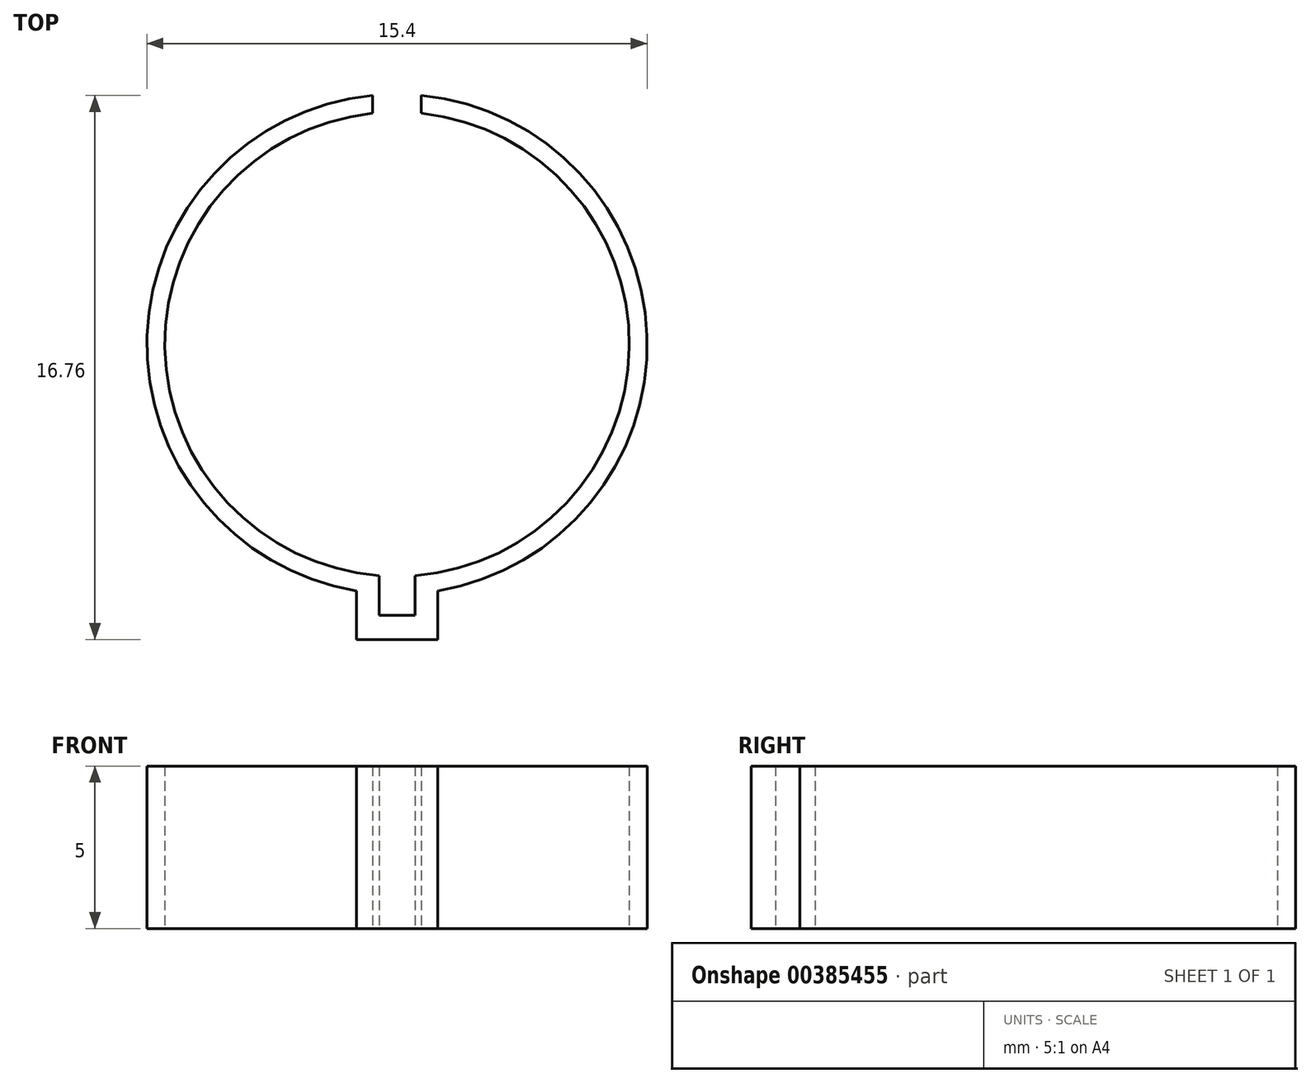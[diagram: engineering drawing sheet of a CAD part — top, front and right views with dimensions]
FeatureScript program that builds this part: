
annotation { "Feature Type Name" : "Feature", "Feature Type Description" : "" }
export const myFeature = defineFeature(function(context is Context, id is Id, definition is map)
    precondition{}
    {
        {
            var Q0;
            Q0=qCreatedBy(makeId("Top.planeOp"),FACE);
            var sketch = newSketch(context, id + "F0", { "sketchPlane" : qUnion([Q0])});
            skCircle(sketch, "E0", {"center": v(0, 0) * mm, "radius": 7.15 * mm});
            skCircle(sketch, "E1", {"center": v(0, 0) * mm, "radius": 7.7 * mm});
            skLineSegment(sketch, "E2", {"start": v(-0.75, 7.11) * mm, "end": v(-0.75, 7.66) * mm});
            skLineSegment(sketch, "E3", {"start": v(0.75, 7.11) * mm, "end": v(0.75, 7.66) * mm});
            skLineSegment(sketch, "E4", {"start": v(-1.25, -7.6) * mm, "end": v(-1.25, -9.1) * mm});
            skLineSegment(sketch, "E5", {"start": v(-1.25, -9.1) * mm, "end": v(1.25, -9.1) * mm});
            skLineSegment(sketch, "E6", {"start": v(1.25, -9.1) * mm, "end": v(1.25, -7.6) * mm});
            skLineSegment(sketch, "E7", {"start": v(-0.55, -7.68) * mm, "end": v(-0.55, -8.35) * mm});
            skPoint(sketch, "E7.endSnap0", {"position": v(-1.25, -8.35) * mm});
            skLineSegment(sketch, "E8", {"start": v(-0.55, -8.35) * mm, "end": v(0.55, -8.35) * mm});
            skPoint(sketch, "E8.endSnap0", {"position": v(1.25, -8.35) * mm});
            skLineSegment(sketch, "E9", {"start": v(0.55, -8.35) * mm, "end": v(0.55, -7.6) * mm});
            skLineSegment(sketch, "E10", {"start": v(0.55, -7.6) * mm, "end": v(0.55, -7.13) * mm});
            skLineSegment(sketch, "E11", {"start": v(-0.55, -7.68) * mm, "end": v(-0.55, -7.13) * mm});
            skSolve(sketch);
        }
        {
            var Q0;
            {var subQ4=sQuery(id+"F0.wireOp",EDGE,"E2");Q0=makeQuery(id+"F0.imprint","IMPRINT",FACE,{"disambiguationData":[TD([[makeQuery(id+"F0.imprint","IMPRINT",EDGE,{"derivedFrom":subQ4}),1.0]])]});}
            var Q1;
            {var subQ0=sQuery(id+"F0.wireOp",EDGE,"E4");Q1=makeQuery(id+"F0.imprint","IMPRINT",FACE,{"disambiguationData":[TD([[makeQuery(id+"F0.imprint","IMPRINT",EDGE,{"derivedFrom":subQ0}),1.0]])]});}
            var Q2;
            {var subQ0=sQuery(id+"F0.wireOp",EDGE,"E3");Q2=makeQuery(id+"F0.imprint","IMPRINT",FACE,{"disambiguationData":[TD([[makeQuery(id+"F0.imprint","IMPRINT",EDGE,{"derivedFrom":subQ0}),-1.0]])]});}
            extrude(context, id + "F1", {"entities" : qUnion([Q0, Q1, Q2]), "depth" : 5 * mm});
        }
    });
